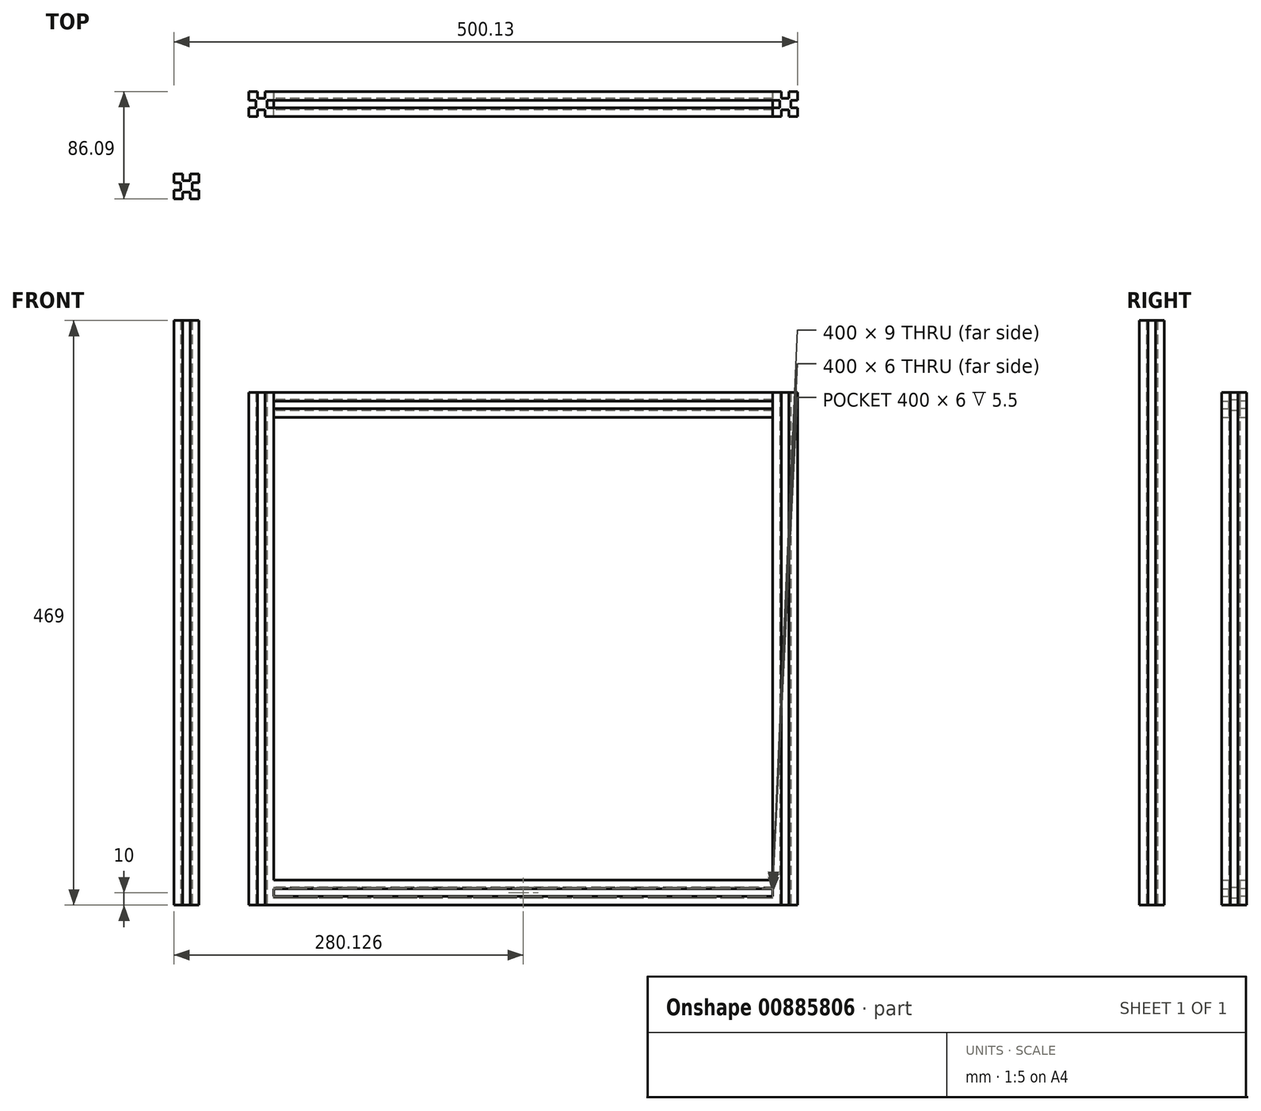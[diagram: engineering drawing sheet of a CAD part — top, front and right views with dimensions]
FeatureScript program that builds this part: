
annotation { "Feature Type Name" : "Feature", "Feature Type Description" : "" }
export const myFeature = defineFeature(function(context is Context, id is Id, definition is map)
    precondition{}
    {
        {
            var Q0;
            Q0=qCreatedBy(makeId("Top.planeOp"),FACE);
            var sketch = newSketch(context, id + "F0", { "sketchPlane" : qUnion([Q0])});
            skLineSegment(sketch, "E0.bottom", {"start": v(-9.97, 9.1) * mm, "end": v(10.03, 9.1) * mm});
            skLineSegment(sketch, "E1.bottom", {"start": v(3.03, 9.1) * mm, "end": v(-2.97, 9.1) * mm});
            skLineSegment(sketch, "E2.bottom", {"start": v(-10, -10.9) * mm, "end": v(10, -10.9) * mm});
            skLineSegment(sketch, "E2.top", {"start": v(-10, 9.1) * mm, "end": v(10, 9.1) * mm});
            skLineSegment(sketch, "E2.left", {"start": v(-10, -10.9) * mm, "end": v(-10, 9.1) * mm});
            skLineSegment(sketch, "E2.right", {"start": v(10, -10.9) * mm, "end": v(10, 9.1) * mm});
            skLineSegment(sketch, "E3.bottom", {"start": v(-3, 9.1) * mm, "end": v(3, 9.1) * mm});
            skLineSegment(sketch, "E3.top", {"start": v(-3, 3.6) * mm, "end": v(3, 3.6) * mm});
            skLineSegment(sketch, "E3.left", {"start": v(-3, 9.1) * mm, "end": v(-3, 3.6) * mm});
            skLineSegment(sketch, "E3.right", {"start": v(3, 9.1) * mm, "end": v(3, 3.6) * mm});
            skLineSegment(sketch, "E4.bottom", {"start": v(10, 2.1) * mm, "end": v(4.5, 2.1) * mm});
            skLineSegment(sketch, "E4.top", {"start": v(10, -3.9) * mm, "end": v(4.5, -3.9) * mm});
            skLineSegment(sketch, "E4.left", {"start": v(10, 2.1) * mm, "end": v(10, -3.9) * mm});
            skLineSegment(sketch, "E4.right", {"start": v(4.5, 2.1) * mm, "end": v(4.5, -3.9) * mm});
            skLineSegment(sketch, "E5.bottom", {"start": v(3, -10.9) * mm, "end": v(-3, -10.9) * mm});
            skLineSegment(sketch, "E5.top", {"start": v(3, -5.4) * mm, "end": v(-3, -5.4) * mm});
            skLineSegment(sketch, "E5.left", {"start": v(3, -10.9) * mm, "end": v(3, -5.4) * mm});
            skLineSegment(sketch, "E5.right", {"start": v(-3, -10.9) * mm, "end": v(-3, -5.4) * mm});
            skLineSegment(sketch, "E6.bottom", {"start": v(-10, -3.9) * mm, "end": v(-4.5, -3.9) * mm});
            skLineSegment(sketch, "E6.top", {"start": v(-10, 2.1) * mm, "end": v(-4.5, 2.1) * mm});
            skLineSegment(sketch, "E6.left", {"start": v(-10, -3.9) * mm, "end": v(-10, 2.1) * mm});
            skLineSegment(sketch, "E6.right", {"start": v(-4.5, -3.9) * mm, "end": v(-4.5, 2.1) * mm});
            skSolve(sketch);
        }
        {
            var Q0;
            Q0=makeQuery(id+"F0.imprint","IMPRINT",FACE,{"disambiguationData":[TD([[makeQuery(id+"F0.imprint","IMPRINT",EDGE,{"derivedFrom":sQuery(id+"F0.wireOp",EDGE,"E3.top")}),-1.0]])]});
            extrude(context, id + "F1", {"entities" : qUnion([Q0]), "depth" : 469 * mm, "offsetDistance" : 25 * mm});
        }
        {
            var Q0;
            Q0=qCreatedBy(makeId("Top.planeOp"),FACE);
            var sketch = newSketch(context, id + "F2", { "sketchPlane" : qUnion([Q0])});
            skLineSegment(sketch, "E7.bottom", {"start": v(50.16, 75.18) * mm, "end": v(70.16, 75.18) * mm});
            skLineSegment(sketch, "E8.bottom", {"start": v(63.16, 75.18) * mm, "end": v(57.16, 75.18) * mm});
            skLineSegment(sketch, "E9.bottom", {"start": v(50.13, 55.18) * mm, "end": v(70.13, 55.18) * mm});
            skLineSegment(sketch, "E9.top", {"start": v(50.13, 75.18) * mm, "end": v(70.13, 75.18) * mm});
            skLineSegment(sketch, "E9.left", {"start": v(50.13, 55.18) * mm, "end": v(50.13, 75.18) * mm});
            skLineSegment(sketch, "E9.right", {"start": v(70.13, 55.18) * mm, "end": v(70.13, 75.18) * mm});
            skLineSegment(sketch, "E10.bottom", {"start": v(57.13, 75.18) * mm, "end": v(63.13, 75.18) * mm});
            skLineSegment(sketch, "E10.top", {"start": v(57.13, 69.68) * mm, "end": v(63.13, 69.68) * mm});
            skLineSegment(sketch, "E10.left", {"start": v(57.13, 75.18) * mm, "end": v(57.13, 69.68) * mm});
            skLineSegment(sketch, "E10.right", {"start": v(63.13, 75.18) * mm, "end": v(63.13, 69.68) * mm});
            skLineSegment(sketch, "E11.bottom", {"start": v(70.13, 68.18) * mm, "end": v(64.63, 68.18) * mm});
            skLineSegment(sketch, "E11.top", {"start": v(70.13, 62.18) * mm, "end": v(64.63, 62.18) * mm});
            skLineSegment(sketch, "E11.left", {"start": v(70.13, 68.18) * mm, "end": v(70.13, 62.18) * mm});
            skLineSegment(sketch, "E11.right", {"start": v(64.63, 68.18) * mm, "end": v(64.63, 62.18) * mm});
            skLineSegment(sketch, "E12.bottom", {"start": v(63.13, 55.18) * mm, "end": v(57.13, 55.18) * mm});
            skLineSegment(sketch, "E12.top", {"start": v(63.13, 60.68) * mm, "end": v(57.13, 60.68) * mm});
            skLineSegment(sketch, "E12.left", {"start": v(63.13, 55.18) * mm, "end": v(63.13, 60.68) * mm});
            skLineSegment(sketch, "E12.right", {"start": v(57.13, 55.18) * mm, "end": v(57.13, 60.68) * mm});
            skLineSegment(sketch, "E13.bottom", {"start": v(50.13, 62.18) * mm, "end": v(55.63, 62.18) * mm});
            skLineSegment(sketch, "E13.top", {"start": v(50.13, 68.18) * mm, "end": v(55.63, 68.18) * mm});
            skLineSegment(sketch, "E13.left", {"start": v(50.13, 62.18) * mm, "end": v(50.13, 68.18) * mm});
            skLineSegment(sketch, "E13.right", {"start": v(55.63, 62.18) * mm, "end": v(55.63, 68.18) * mm});
            skSolve(sketch);
        }
        {
            var Q0;
            Q0=makeQuery(id+"F2.imprint","IMPRINT",FACE,{"disambiguationData":[TD([[makeQuery(id+"F2.imprint","IMPRINT",EDGE,{"derivedFrom":sQuery(id+"F2.wireOp",EDGE,"E10.top")}),-1.0]])]});
            extrude(context, id + "F3", {"entities" : qUnion([Q0]), "depth" : 411.15 * mm, "offsetDistance" : 25 * mm});
        }
        {
            var Q0;
            {var subQ0=sQuery(id+"F2.wireOp",EDGE,"E9.right");Q0=makeQuery(id+"F3.opExtrude","SWEPT_FACE",FACE,{"disambiguationData":[OSD([subQ0]),TDD([makeQuery(id+"F2.imprint","IMPRINT",EDGE,{"disambiguationData":[TD([[makeQuery(id+"F2.imprint","INTERSECT",VERTEX,{"derivedFrom":[sQuery(id+"F2.wireOp",EDGE,"E9.top"),subQ0]}),1.0]])],"derivedFrom":subQ0})])]});}
            var sketch = newSketch(context, id + "F4", { "sketchPlane" : qUnion([Q0])});
            skLineSegment(sketch, "E14.bottom", {"start": v(55.21, 20) * mm, "end": v(75.21, 20) * mm});
            skLineSegment(sketch, "E15.bottom", {"start": v(68.21, 20) * mm, "end": v(62.21, 20) * mm});
            skLineSegment(sketch, "E16.bottom", {"start": v(55.18, 0) * mm, "end": v(75.18, 0) * mm});
            skLineSegment(sketch, "E16.top", {"start": v(55.18, 20) * mm, "end": v(75.18, 20) * mm});
            skLineSegment(sketch, "E16.left", {"start": v(55.18, 0) * mm, "end": v(55.18, 20) * mm});
            skLineSegment(sketch, "E16.right", {"start": v(75.18, 0) * mm, "end": v(75.18, 20) * mm});
            skLineSegment(sketch, "E17.bottom", {"start": v(62.18, 20) * mm, "end": v(68.18, 20) * mm});
            skLineSegment(sketch, "E17.top", {"start": v(62.18, 14.5) * mm, "end": v(68.18, 14.5) * mm});
            skLineSegment(sketch, "E17.left", {"start": v(62.18, 20) * mm, "end": v(62.18, 14.5) * mm});
            skLineSegment(sketch, "E17.right", {"start": v(68.18, 20) * mm, "end": v(68.18, 14.5) * mm});
            skLineSegment(sketch, "E18.bottom", {"start": v(75.18, 13) * mm, "end": v(69.68, 13) * mm});
            skLineSegment(sketch, "E18.top", {"start": v(75.18, 7) * mm, "end": v(69.68, 7) * mm});
            skLineSegment(sketch, "E18.left", {"start": v(75.18, 13) * mm, "end": v(75.18, 7) * mm});
            skLineSegment(sketch, "E18.right", {"start": v(69.68, 13) * mm, "end": v(69.68, 7) * mm});
            skLineSegment(sketch, "E19.bottom", {"start": v(68.18, 0) * mm, "end": v(62.18, 0) * mm});
            skLineSegment(sketch, "E19.top", {"start": v(68.18, 5.5) * mm, "end": v(62.18, 5.5) * mm});
            skLineSegment(sketch, "E19.left", {"start": v(68.18, 0) * mm, "end": v(68.18, 5.5) * mm});
            skLineSegment(sketch, "E19.right", {"start": v(62.18, 0) * mm, "end": v(62.18, 5.5) * mm});
            skLineSegment(sketch, "E20.bottom", {"start": v(55.18, 7) * mm, "end": v(60.68, 7) * mm});
            skLineSegment(sketch, "E20.top", {"start": v(55.18, 13) * mm, "end": v(60.68, 13) * mm});
            skLineSegment(sketch, "E20.left", {"start": v(55.18, 7) * mm, "end": v(55.18, 13) * mm});
            skLineSegment(sketch, "E20.right", {"start": v(60.68, 7) * mm, "end": v(60.68, 13) * mm});
            skLineSegment(sketch, "E21.bottom", {"start": v(55.24, 411.16) * mm, "end": v(75.24, 411.16) * mm});
            skLineSegment(sketch, "E22.bottom", {"start": v(68.24, 411.16) * mm, "end": v(62.24, 411.16) * mm});
            skLineSegment(sketch, "E23.bottom", {"start": v(55.2, 391.16) * mm, "end": v(75.2, 391.16) * mm});
            skLineSegment(sketch, "E23.top", {"start": v(55.2, 411.16) * mm, "end": v(75.2, 411.16) * mm});
            skLineSegment(sketch, "E23.left", {"start": v(55.2, 391.16) * mm, "end": v(55.2, 411.16) * mm});
            skLineSegment(sketch, "E23.right", {"start": v(75.2, 391.16) * mm, "end": v(75.2, 411.16) * mm});
            skLineSegment(sketch, "E24.bottom", {"start": v(62.2, 411.16) * mm, "end": v(68.2, 411.16) * mm});
            skLineSegment(sketch, "E24.top", {"start": v(62.2, 405.66) * mm, "end": v(68.2, 405.66) * mm});
            skLineSegment(sketch, "E24.left", {"start": v(62.2, 411.16) * mm, "end": v(62.2, 405.66) * mm});
            skLineSegment(sketch, "E24.right", {"start": v(68.2, 411.16) * mm, "end": v(68.2, 405.66) * mm});
            skLineSegment(sketch, "E25.bottom", {"start": v(75.2, 404.16) * mm, "end": v(69.7, 404.16) * mm});
            skLineSegment(sketch, "E25.top", {"start": v(75.2, 398.16) * mm, "end": v(69.7, 398.16) * mm});
            skLineSegment(sketch, "E25.left", {"start": v(75.2, 404.16) * mm, "end": v(75.2, 398.16) * mm});
            skLineSegment(sketch, "E25.right", {"start": v(69.7, 404.16) * mm, "end": v(69.7, 398.16) * mm});
            skLineSegment(sketch, "E26.bottom", {"start": v(68.2, 391.16) * mm, "end": v(62.2, 391.16) * mm});
            skLineSegment(sketch, "E26.top", {"start": v(68.2, 396.66) * mm, "end": v(62.2, 396.66) * mm});
            skLineSegment(sketch, "E26.left", {"start": v(68.2, 391.16) * mm, "end": v(68.2, 396.66) * mm});
            skLineSegment(sketch, "E26.right", {"start": v(62.2, 391.16) * mm, "end": v(62.2, 396.66) * mm});
            skLineSegment(sketch, "E27.bottom", {"start": v(55.2, 398.16) * mm, "end": v(60.7, 398.16) * mm});
            skLineSegment(sketch, "E27.top", {"start": v(55.2, 404.16) * mm, "end": v(60.7, 404.16) * mm});
            skLineSegment(sketch, "E27.left", {"start": v(55.2, 398.16) * mm, "end": v(55.2, 404.16) * mm});
            skLineSegment(sketch, "E27.right", {"start": v(60.7, 398.16) * mm, "end": v(60.7, 404.16) * mm});
            skSolve(sketch);
        }
        {
            var Q0;
            {var subQ4=sQuery(id+"F4.wireOp",EDGE,"E24.left");Q0=makeQuery(id+"F4.imprint","IMPRINT",FACE,{"disambiguationData":[TD([[makeQuery(id+"F4.imprint","IMPRINT",EDGE,{"derivedFrom":subQ4}),-1.0]])]});}
            var Q1;
            {var subQ9=sQuery(id+"F4.wireOp",EDGE,"E25.right");Q1=makeQuery(id+"F4.imprint","IMPRINT",FACE,{"disambiguationData":[TD([[makeQuery(id+"F4.imprint","IMPRINT",EDGE,{"derivedFrom":subQ9}),-1.0]])]});}
            var Q2;
            {var subQ7=sQuery(id+"F4.wireOp",EDGE,"E17.right");Q2=makeQuery(id+"F4.imprint","IMPRINT",FACE,{"disambiguationData":[TD([[makeQuery(id+"F4.imprint","IMPRINT",EDGE,{"derivedFrom":subQ7}),1.0]])]});}
            var Q3;
            {var subQ3=sQuery(id+"F4.wireOp",EDGE,"E17.top");Q3=makeQuery(id+"F4.imprint","IMPRINT",FACE,{"disambiguationData":[TD([[makeQuery(id+"F4.imprint","IMPRINT",EDGE,{"derivedFrom":subQ3}),-1.0]])]});}
            extrude(context, id + "F5", {"entities" : qUnion([Q0, Q1, Q2, Q3]), "operationType" : NewBodyOperationType.ADD, "depth" : 400 * mm, "offsetDistance" : 25 * mm});
        }
        {
            var Q0;
            {var subQ0=sQuery(id+"F4.wireOp",EDGE,"E16.bottom");Q0=makeQuery(id+"F5.boolean.opBoolean","MERGE",FACE,{"derivedFrom":[makeQuery(id+"F3.opExtrude","CAP_FACE",FACE,{"disambiguationData":[OSD([sQuery(id+"F2.wireOp",EDGE,"E9.bottom"),sQuery(id+"F2.wireOp",EDGE,"E9.top"),sQuery(id+"F2.wireOp",EDGE,"E9.left"),sQuery(id+"F2.wireOp",EDGE,"E9.right"),sQuery(id+"F2.wireOp",EDGE,"E10.top"),sQuery(id+"F2.wireOp",EDGE,"E10.left"),sQuery(id+"F2.wireOp",EDGE,"E10.right"),sQuery(id+"F2.wireOp",EDGE,"E11.bottom"),sQuery(id+"F2.wireOp",EDGE,"E11.top"),sQuery(id+"F2.wireOp",EDGE,"E11.right"),sQuery(id+"F2.wireOp",EDGE,"E12.top"),sQuery(id+"F2.wireOp",EDGE,"E12.left"),sQuery(id+"F2.wireOp",EDGE,"E12.right"),sQuery(id+"F2.wireOp",EDGE,"E13.bottom"),sQuery(id+"F2.wireOp",EDGE,"E13.top"),sQuery(id+"F2.wireOp",EDGE,"E13.right")])],"isStart":true}),makeQuery(id+"F5.opExtrude","SWEPT_FACE",FACE,{"disambiguationData":[OSD([subQ0]),TDD([makeQuery(id+"F4.imprint","IMPRINT",EDGE,{"disambiguationData":[TD([[makeQuery(id+"F4.imprint","INTERSECT",VERTEX,{"derivedFrom":[subQ0,sQuery(id+"F4.wireOp",EDGE,"E16.left")]}),-1.0]])],"derivedFrom":subQ0})])]}),makeQuery(id+"F5.opExtrude","SWEPT_FACE",FACE,{"disambiguationData":[OSD([subQ0]),TDD([makeQuery(id+"F4.imprint","IMPRINT",EDGE,{"disambiguationData":[TD([[makeQuery(id+"F4.imprint","INTERSECT",VERTEX,{"derivedFrom":[subQ0,sQuery(id+"F4.wireOp",EDGE,"E16.right")]}),1.0]])],"derivedFrom":subQ0})])]})]});}
            var sketch = newSketch(context, id + "F6", { "sketchPlane" : qUnion([Q0])});
            skLineSegment(sketch, "E28.bottom", {"start": v(470.16, -55.18) * mm, "end": v(490.16, -55.18) * mm});
            skLineSegment(sketch, "E29.bottom", {"start": v(483.16, -55.18) * mm, "end": v(477.16, -55.18) * mm});
            skLineSegment(sketch, "E30.bottom", {"start": v(470.13, -75.18) * mm, "end": v(490.13, -75.18) * mm});
            skLineSegment(sketch, "E30.top", {"start": v(470.13, -55.18) * mm, "end": v(490.13, -55.18) * mm});
            skLineSegment(sketch, "E30.left", {"start": v(470.13, -75.18) * mm, "end": v(470.13, -55.18) * mm});
            skLineSegment(sketch, "E30.right", {"start": v(490.13, -75.18) * mm, "end": v(490.13, -55.18) * mm});
            skLineSegment(sketch, "E31.bottom", {"start": v(477.13, -55.18) * mm, "end": v(483.13, -55.18) * mm});
            skLineSegment(sketch, "E31.top", {"start": v(477.13, -60.68) * mm, "end": v(483.13, -60.68) * mm});
            skLineSegment(sketch, "E31.left", {"start": v(477.13, -55.18) * mm, "end": v(477.13, -60.68) * mm});
            skLineSegment(sketch, "E31.right", {"start": v(483.13, -55.18) * mm, "end": v(483.13, -60.68) * mm});
            skLineSegment(sketch, "E32.bottom", {"start": v(490.13, -62.18) * mm, "end": v(484.63, -62.18) * mm});
            skLineSegment(sketch, "E32.top", {"start": v(490.13, -68.18) * mm, "end": v(484.63, -68.18) * mm});
            skLineSegment(sketch, "E32.left", {"start": v(490.13, -62.18) * mm, "end": v(490.13, -68.18) * mm});
            skLineSegment(sketch, "E32.right", {"start": v(484.63, -62.18) * mm, "end": v(484.63, -68.18) * mm});
            skLineSegment(sketch, "E33.bottom", {"start": v(483.13, -75.18) * mm, "end": v(477.13, -75.18) * mm});
            skLineSegment(sketch, "E33.top", {"start": v(483.13, -69.68) * mm, "end": v(477.13, -69.68) * mm});
            skLineSegment(sketch, "E33.left", {"start": v(483.13, -75.18) * mm, "end": v(483.13, -69.68) * mm});
            skLineSegment(sketch, "E33.right", {"start": v(477.13, -75.18) * mm, "end": v(477.13, -69.68) * mm});
            skLineSegment(sketch, "E34.bottom", {"start": v(470.13, -68.18) * mm, "end": v(475.63, -68.18) * mm});
            skLineSegment(sketch, "E34.top", {"start": v(470.13, -62.18) * mm, "end": v(475.63, -62.18) * mm});
            skLineSegment(sketch, "E34.left", {"start": v(470.13, -68.18) * mm, "end": v(470.13, -62.18) * mm});
            skLineSegment(sketch, "E34.right", {"start": v(475.63, -68.18) * mm, "end": v(475.63, -62.18) * mm});
            skSolve(sketch);
        }
        {
            var Q0;
            Q0=makeQuery(id+"F6.imprint","IMPRINT",FACE,{"disambiguationData":[TD([[makeQuery(id+"F6.imprint","IMPRINT",EDGE,{"derivedFrom":sQuery(id+"F6.wireOp",EDGE,"E31.top")}),-1.0]])]});
            extrude(context, id + "F7", {"entities" : qUnion([Q0]), "operationType" : NewBodyOperationType.ADD, "oppositeDirection" : true, "depth" : 411.15 * mm, "offsetDistance" : 25 * mm});
        }
    });
